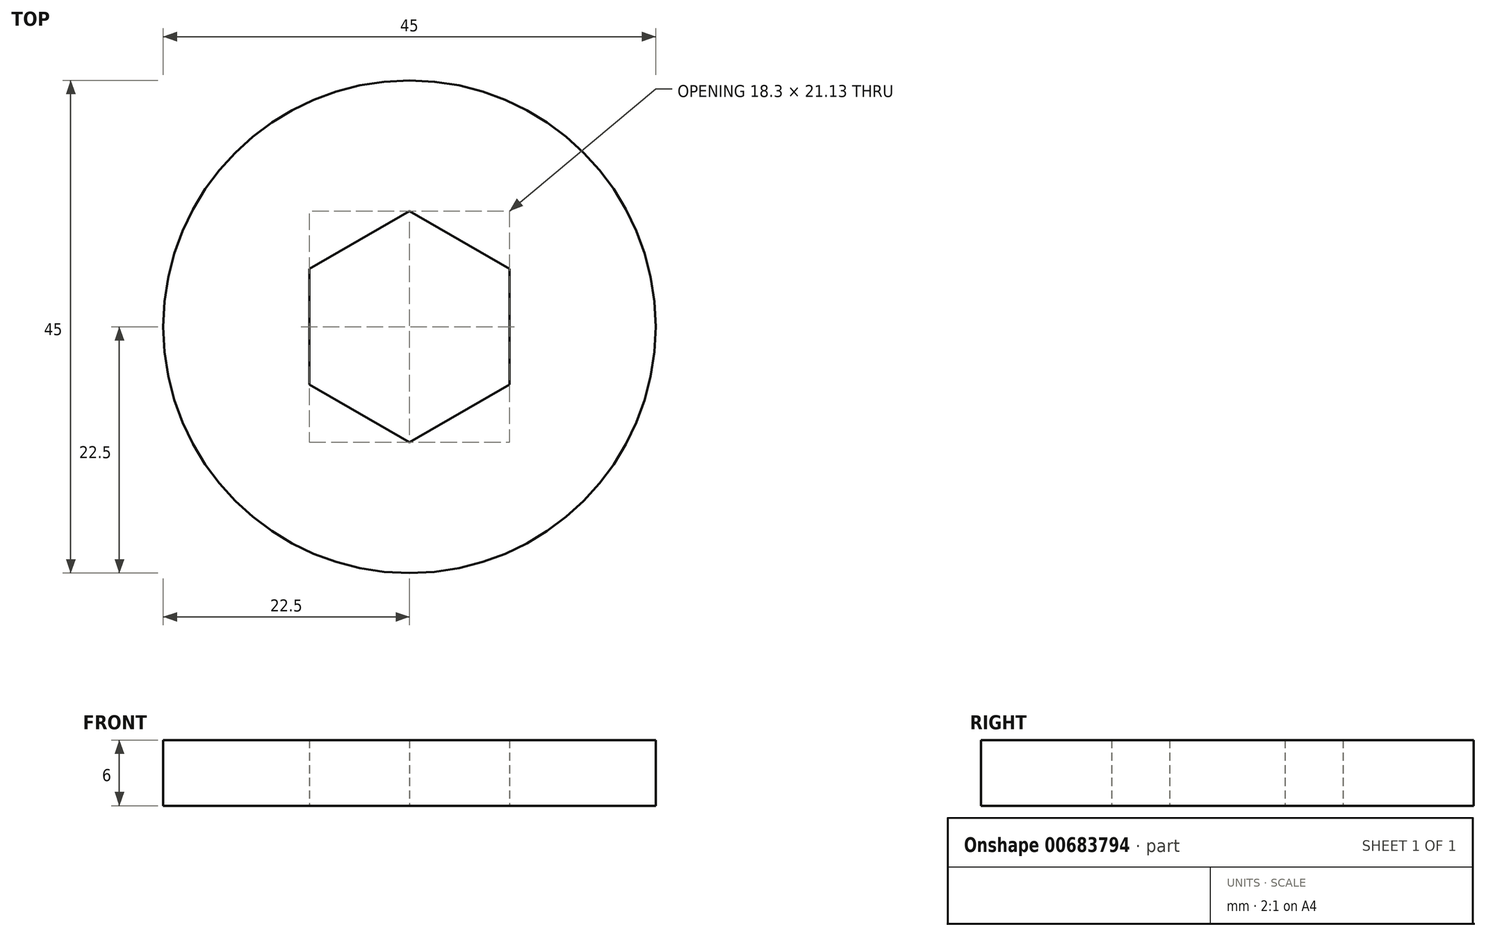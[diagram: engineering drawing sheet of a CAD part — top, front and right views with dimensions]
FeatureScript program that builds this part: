
annotation { "Feature Type Name" : "Feature", "Feature Type Description" : "" }
export const myFeature = defineFeature(function(context is Context, id is Id, definition is map)
    precondition{}
    {
        {
            var Q0;
            Q0=qCreatedBy(makeId("Top.planeOp"),FACE);
            var sketch = newSketch(context, id + "F0", { "sketchPlane" : qUnion([Q0])});
            skCircle(sketch, "E0", {"center": v(0, 0) * mm, "radius": 22.5 * mm});
            skCircle(sketch, "E1.cCircle", {"center": v(0, 0) * mm, "radius": 9.15 * mm, "construction": true});
            skLineSegment(sketch, "E1.0", {"start": v(-9.15, -5.28) * mm, "end": v(-9.15, 5.28) * mm});
            skLineSegment(sketch, "E1.1", {"start": v(-9.15, 5.28) * mm, "end": v(0, 10.57) * mm});
            skLineSegment(sketch, "E1.2", {"start": v(0, 10.57) * mm, "end": v(9.15, 5.28) * mm});
            skLineSegment(sketch, "E1.3", {"start": v(9.15, 5.28) * mm, "end": v(9.15, -5.28) * mm});
            skLineSegment(sketch, "E1.4", {"start": v(9.15, -5.28) * mm, "end": v(0, -10.57) * mm});
            skLineSegment(sketch, "E1.5", {"start": v(0, -10.57) * mm, "end": v(-9.15, -5.28) * mm});
            skPoint(sketch, "E1.0.midPoint", {"position": v(-9.15, 0) * mm});
            skSolve(sketch);
        }
        {
            var Q0;
            Q0=makeQuery(id+"F0.imprint","IMPRINT",FACE,{"disambiguationData":[TD([[makeQuery(id+"F0.imprint","IMPRINT",EDGE,{"derivedFrom":sQuery(id+"F0.wireOp",EDGE,"E0")}),1.0]])]});
            extrude(context, id + "F1", {"entities" : qUnion([Q0]), "depth" : 6 * mm, "offsetDistance" : 25 * mm});
        }
    });
